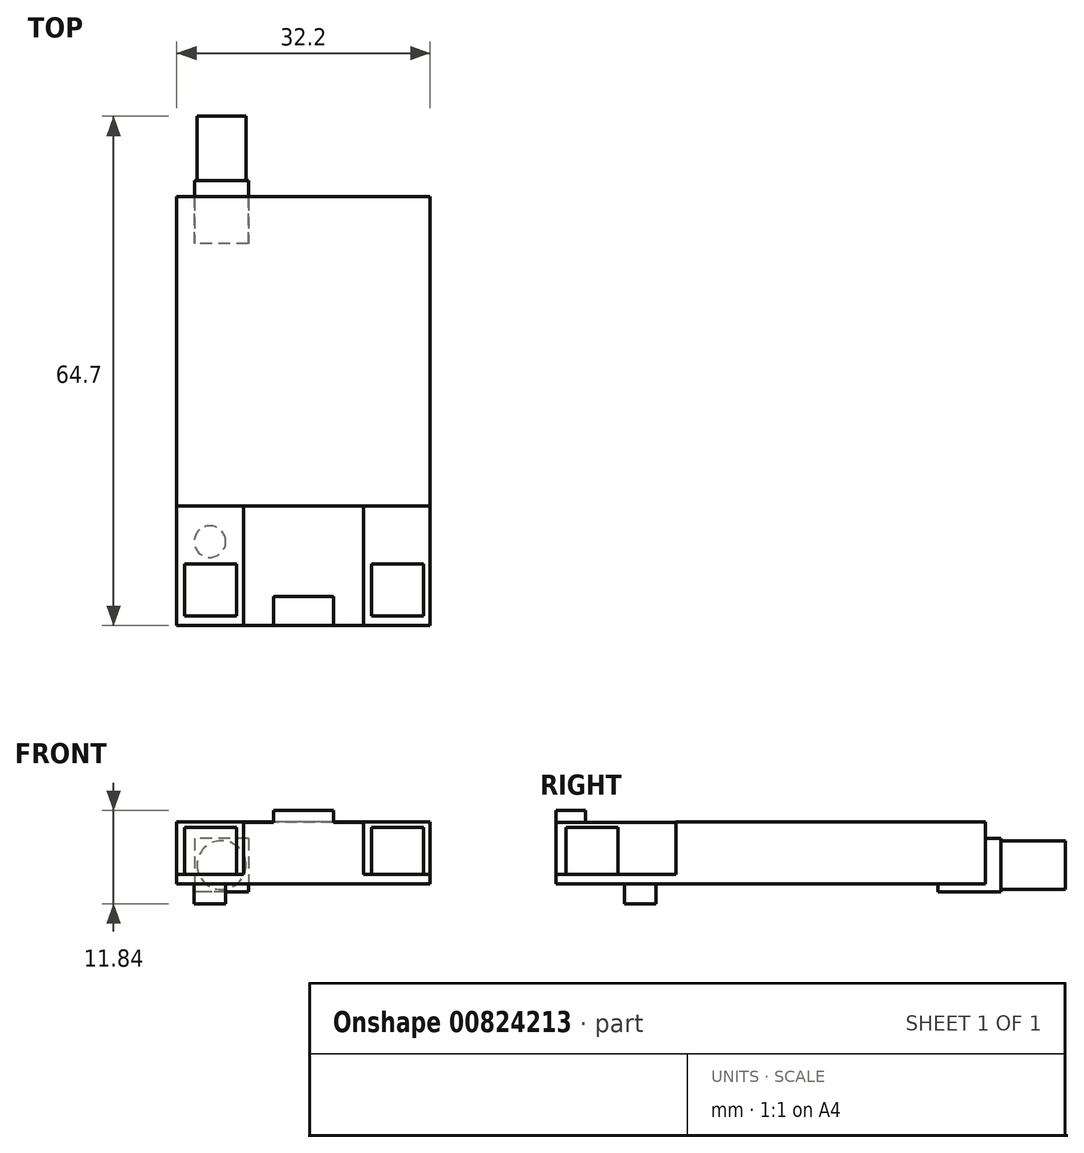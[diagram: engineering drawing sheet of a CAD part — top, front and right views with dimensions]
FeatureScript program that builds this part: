
annotation { "Feature Type Name" : "Feature", "Feature Type Description" : "" }
export const myFeature = defineFeature(function(context is Context, id is Id, definition is map)
    precondition{}
    {
        {
            var Q0;
            Q0=qCreatedBy(makeId("Top.planeOp"),FACE);
            var sketch = newSketch(context, id + "F0", { "sketchPlane" : qUnion([Q0])});
            skLineSegment(sketch, "E0.bottom", {"start": v(16.1, -27.25) * mm, "end": v(-16.1, -27.25) * mm});
            skLineSegment(sketch, "E0.top", {"start": v(16.1, 27.25) * mm, "end": v(-16.1, 27.25) * mm});
            skLineSegment(sketch, "E0.left", {"start": v(16.1, -27.25) * mm, "end": v(16.1, 27.25) * mm});
            skLineSegment(sketch, "E0.right", {"start": v(-16.1, -27.25) * mm, "end": v(-16.1, 27.25) * mm});
            skPoint(sketch, "E0.middle", {"position": v(0, 0) * mm});
            skSolve(sketch);
        }
        {
            var Q0;
            Q0=makeQuery(id+"F0.imprint","IMPRINT",FACE,{"disambiguationData":[TD([[makeQuery(id+"F0.imprint","IMPRINT",EDGE,{"derivedFrom":sQuery(id+"F0.wireOp",EDGE,"E0.bottom")}),-1.0]])]});
            extrude(context, id + "F1", {"entities" : qUnion([Q0]), "depth" : 1.2 * mm, "offsetDistance" : 25 * mm});
        }
        {
            var Q0;
            Q0=makeQuery(id+"F1.opExtrude","CAP_FACE",FACE,{"disambiguationData":[OSD([sQuery(id+"F0.wireOp",EDGE,"E0.bottom"),sQuery(id+"F0.wireOp",EDGE,"E0.top"),sQuery(id+"F0.wireOp",EDGE,"E0.left"),sQuery(id+"F0.wireOp",EDGE,"E0.right")])],"isStart":false});
            var sketch = newSketch(context, id + "F2", { "sketchPlane" : qUnion([Q0])});
            skLineSegment(sketch, "E1.bottom", {"start": v(-8.52, -26.02) * mm, "end": v(-15.12, -26.02) * mm});
            skLineSegment(sketch, "E1.top", {"start": v(-8.52, -19.42) * mm, "end": v(-15.12, -19.42) * mm});
            skLineSegment(sketch, "E1.left", {"start": v(-8.52, -26.02) * mm, "end": v(-8.52, -19.42) * mm});
            skLineSegment(sketch, "E1.right", {"start": v(-15.12, -26.02) * mm, "end": v(-15.12, -19.42) * mm});
            skPoint(sketch, "E1.middle", {"position": v(-11.82, -22.72) * mm});
            skLineSegment(sketch, "E2.bottom", {"start": v(15.27, -26.02) * mm, "end": v(8.67, -26.02) * mm});
            skLineSegment(sketch, "E2.top", {"start": v(15.27, -19.42) * mm, "end": v(8.67, -19.42) * mm});
            skLineSegment(sketch, "E2.left", {"start": v(15.27, -26.02) * mm, "end": v(15.27, -19.42) * mm});
            skLineSegment(sketch, "E2.right", {"start": v(8.67, -26.02) * mm, "end": v(8.67, -19.42) * mm});
            skPoint(sketch, "E2.middle", {"position": v(11.97, -22.72) * mm});
            skLineSegment(sketch, "E3.bottom", {"start": v(7.62, -27.25) * mm, "end": v(-7.61, -27.25) * mm});
            skLineSegment(sketch, "E3.top", {"start": v(7.62, -12.05) * mm, "end": v(-7.62, -12.05) * mm});
            skLineSegment(sketch, "E3.left", {"start": v(7.62, -27.25) * mm, "end": v(7.61, -12.05) * mm});
            skLineSegment(sketch, "E3.right", {"start": v(-7.61, -27.25) * mm, "end": v(-7.62, -12.05) * mm});
            skPoint(sketch, "E3.middle", {"position": v(0, -19.65) * mm});
            skLineSegment(sketch, "E4.bottom", {"start": v(-16.1, 27.25) * mm, "end": v(16.1, 27.25) * mm});
            skLineSegment(sketch, "E4.top", {"start": v(-16.1, -12.05) * mm, "end": v(16.1, -12.05) * mm});
            skLineSegment(sketch, "E4.left", {"start": v(-16.1, 27.25) * mm, "end": v(-16.1, -12.05) * mm});
            skLineSegment(sketch, "E4.right", {"start": v(16.1, 27.25) * mm, "end": v(16.1, -12.05) * mm});
            skSolve(sketch);
        }
        {
            var Q0;
            Q0=makeQuery(id+"F2.imprint","IMPRINT",FACE,{"disambiguationData":[TD([[makeQuery(id+"F2.imprint","IMPRINT",EDGE,{"derivedFrom":sQuery(id+"F2.wireOp",EDGE,"E4.bottom")}),1.0]])]});
            extrude(context, id + "F3", {"entities" : qUnion([Q0]), "operationType" : NewBodyOperationType.ADD, "depth" : (7.9 - 1.2) * mm, "offsetDistance" : 25 * mm});
        }
        {
            var Q0;
            Q0=makeQuery(id+"F2.imprint","IMPRINT",FACE,{"disambiguationData":[TD([[makeQuery(id+"F2.imprint","IMPRINT",EDGE,{"derivedFrom":sQuery(id+"F2.wireOp",EDGE,"E3.bottom")}),-1.0]])]});
            extrude(context, id + "F4", {"entities" : qUnion([Q0]), "operationType" : NewBodyOperationType.ADD, "depth" : 8.14 * mm, "offsetDistance" : 25 * mm});
        }
        {
            var Q0;
            Q0=makeQuery(id+"F2.imprint","IMPRINT",FACE,{"disambiguationData":[TD([[makeQuery(id+"F2.imprint","IMPRINT",EDGE,{"derivedFrom":sQuery(id+"F2.wireOp",EDGE,"E1.bottom")}),-1.0]])]});
            var Q1;
            Q1=makeQuery(id+"F2.imprint","IMPRINT",FACE,{"disambiguationData":[TD([[makeQuery(id+"F2.imprint","IMPRINT",EDGE,{"derivedFrom":sQuery(id+"F2.wireOp",EDGE,"E2.bottom")}),-1.0]])]});
            extrude(context, id + "F5", {"entities" : qUnion([Q0, Q1]), "operationType" : NewBodyOperationType.ADD, "depth" : 6 * mm, "offsetDistance" : 25 * mm});
        }
        {
            var Q0;
            Q0=makeQuery(id+"F1.opExtrude","CAP_FACE",FACE,{"disambiguationData":[OSD([sQuery(id+"F0.wireOp",EDGE,"E0.bottom"),sQuery(id+"F0.wireOp",EDGE,"E0.top"),sQuery(id+"F0.wireOp",EDGE,"E0.left"),sQuery(id+"F0.wireOp",EDGE,"E0.right")])],"isStart":true});
            var sketch = newSketch(context, id + "F6", { "sketchPlane" : qUnion([Q0])});
            skCircle(sketch, "E5", {"center": v(-11.88, 16.6) * mm, "radius": 2 * mm});
            skSolve(sketch);
        }
        {
            var Q0;
            Q0=makeQuery(id+"F6.imprint","IMPRINT",FACE,{"disambiguationData":[TD([[makeQuery(id+"F6.imprint","IMPRINT",EDGE,{"derivedFrom":sQuery(id+"F6.wireOp",EDGE,"E5")}),1.0]])]});
            extrude(context, id + "F7", {"entities" : qUnion([Q0]), "operationType" : NewBodyOperationType.ADD, "depth" : 2.5 * mm, "offsetDistance" : 25 * mm});
        }
        {
            var Q0;
            Q0=makeQuery(id+"F3.boolean.opBoolean","MERGE",FACE,{"derivedFrom":[makeQuery(id+"F1.opExtrude","SWEPT_FACE",FACE,{"disambiguationData":[OSD([sQuery(id+"F0.wireOp",EDGE,"E0.top")])]}),makeQuery(id+"F3.opExtrude","SWEPT_FACE",FACE,{"disambiguationData":[OSD([sQuery(id+"F2.wireOp",EDGE,"E4.bottom")])]})]});
            var sketch = newSketch(context, id + "F8", { "sketchPlane" : qUnion([Q0])});
            skLineSegment(sketch, "E6.bottom", {"start": v(7, 5.8) * mm, "end": v(13.8, 5.8) * mm});
            skLineSegment(sketch, "E6.top", {"start": v(7, -1) * mm, "end": v(13.8, -1) * mm});
            skLineSegment(sketch, "E6.left", {"start": v(7, 5.8) * mm, "end": v(7, -1) * mm});
            skLineSegment(sketch, "E6.right", {"start": v(13.8, 5.8) * mm, "end": v(13.8, -1) * mm});
            skCircle(sketch, "E7", {"center": v(10.4, 2.4) * mm, "radius": 3.1 * mm});
            skPoint(sketch, "E7.centerSnap0", {"position": v(7, 2.4) * mm});
            skPoint(sketch, "E7.centerSnap1", {"position": v(10.4, 5.8) * mm});
            skSolve(sketch);
        }
        {
            var Q0;
            {var subQ0=sQuery(id+"F8.wireOp",EDGE,"E7");var subQ1=makeQuery(id+"F1.opExtrude","CAP_EDGE",EDGE,{"disambiguationData":[OSD([sQuery(id+"F0.wireOp",EDGE,"E0.top")])],"isStart":true});var subQ2=makeQuery(id+"F8.imprint","INTERSECT",VERTEX,{"disambiguationData":[OD(0.0)],"derivedFrom":[subQ1,subQ0]});Q0=makeQuery(id+"F8.imprint","IMPRINT",FACE,{"disambiguationData":[TD([[makeQuery(id+"F8.imprint","IMPRINT",EDGE,{"disambiguationData":[TD([[subQ2,1.0]])],"derivedFrom":subQ0}),1.0]])]});}
            var Q1;
            {var subQ0=sQuery(id+"F8.wireOp",EDGE,"E7");var subQ1=makeQuery(id+"F1.opExtrude","CAP_EDGE",EDGE,{"disambiguationData":[OSD([sQuery(id+"F0.wireOp",EDGE,"E0.top")])],"isStart":true});var subQ2=makeQuery(id+"F8.imprint","INTERSECT",VERTEX,{"disambiguationData":[OD(0.0)],"derivedFrom":[subQ1,subQ0]});Q1=makeQuery(id+"F8.imprint","IMPRINT",FACE,{"disambiguationData":[TD([[makeQuery(id+"F8.imprint","IMPRINT",EDGE,{"disambiguationData":[TD([[subQ2,-1.0]])],"derivedFrom":subQ0}),1.0]])]});}
            extrude(context, id + "F9", {"entities" : qUnion([Q0, Q1]), "operationType" : NewBodyOperationType.ADD, "depth" : 10.2 * mm, "offsetDistance" : 25 * mm});
        }
        {
            var Q0;
            {var subQ1=sQuery(id+"F8.wireOp",EDGE,"E6.top");Q0=makeQuery(id+"F8.imprint","IMPRINT",FACE,{"disambiguationData":[TD([[makeQuery(id+"F8.imprint","IMPRINT",EDGE,{"derivedFrom":subQ1}),1.0]])]});}
            var Q1;
            {var subQ1=sQuery(id+"F8.wireOp",EDGE,"E6.bottom");Q1=makeQuery(id+"F8.imprint","IMPRINT",FACE,{"disambiguationData":[TD([[makeQuery(id+"F8.imprint","IMPRINT",EDGE,{"derivedFrom":subQ1}),-1.0]])]});}
            var Q2;
            Q2=sQuery(id+"F8.wireOp",EDGE,"E7");
            extrude(context, id + "F10", {"entities" : qUnion([Q0, Q1]), "operationType" : NewBodyOperationType.ADD, "surfaceEntities" : qUnion([Q2]), "depth" : 2 * mm, "offsetDistance" : 25 * mm});
        }
        {
            var Q0;
            {var subQ1=sQuery(id+"F8.wireOp",EDGE,"E6.top");Q0=makeQuery(id+"F8.imprint","IMPRINT",FACE,{"disambiguationData":[TD([[makeQuery(id+"F8.imprint","IMPRINT",EDGE,{"derivedFrom":subQ1}),1.0]])]});}
            var Q1;
            {var subQ0=sQuery(id+"F8.wireOp",EDGE,"E7");var subQ1=makeQuery(id+"F1.opExtrude","CAP_EDGE",EDGE,{"disambiguationData":[OSD([sQuery(id+"F0.wireOp",EDGE,"E0.top")])],"isStart":true});var subQ2=makeQuery(id+"F8.imprint","INTERSECT",VERTEX,{"disambiguationData":[OD(0.0)],"derivedFrom":[subQ1,subQ0]});Q1=makeQuery(id+"F8.imprint","IMPRINT",FACE,{"disambiguationData":[TD([[makeQuery(id+"F8.imprint","IMPRINT",EDGE,{"disambiguationData":[TD([[subQ2,-1.0]])],"derivedFrom":subQ0}),1.0]])]});}
            extrude(context, id + "F11", {"entities" : qUnion([Q0, Q1]), "operationType" : NewBodyOperationType.ADD, "oppositeDirection" : true, "depth" : 6 * mm, "offsetDistance" : 25 * mm});
        }
        {
            var Q0;
            Q0=makeQuery(id+"F4.opExtrude","CAP_FACE",FACE,{"disambiguationData":[OSD([sQuery(id+"F2.wireOp",EDGE,"E3.bottom"),sQuery(id+"F2.wireOp",EDGE,"E3.left"),sQuery(id+"F2.wireOp",EDGE,"E3.right"),sQuery(id+"F2.wireOp",EDGE,"E4.top")])],"isStart":false});
            var sketch = newSketch(context, id + "F12", { "sketchPlane" : qUnion([Q0])});
            skLineSegment(sketch, "E8", {"start": v(-3.8, -27.25) * mm, "end": v(-3.8, -23.55) * mm});
            skLineSegment(sketch, "E9", {"start": v(-3.8, -23.55) * mm, "end": v(3.8, -23.55) * mm});
            skLineSegment(sketch, "E10", {"start": v(3.8, -23.55) * mm, "end": v(3.8, -27.25) * mm});
            skLineSegment(sketch, "E11", {"start": v(0, -27.25) * mm, "end": v(0, -20.11) * mm, "construction": true});
            skSolve(sketch);
        }
        {
            var Q0;
            {var subQ2=sQuery(id+"F12.wireOp",EDGE,"E8");Q0=makeQuery(id+"F12.imprint","IMPRINT",FACE,{"disambiguationData":[TD([[makeQuery(id+"F12.imprint","IMPRINT",EDGE,{"derivedFrom":subQ2}),1.0]])]});}
            extrude(context, id + "F13", {"entities" : qUnion([Q0]), "operationType" : NewBodyOperationType.REMOVE, "oppositeDirection" : true, "depth" : 1.5 * mm, "offsetDistance" : 25 * mm});
        }
    });
